# Revit family: Security_MasterStation_AiPhone_GT-C-H
name_source: partatom
category: Generic Models
units: mm (PartAtom-declared; Revit-internal decimal feet)

## family parameters
Can host rebar = No
Classification Number = 23.85.30.11.27
Cut with Voids When Loaded = No
Host = Face
Maintain Annotation Orientation = No
Part Type = Normal
Room Calculation Point = No
Round Connector Dimension = Use Diameter
Shared = No

## types (9) — shared parameters
Assembly Code = D5030900
Camera Control Material = Plastic - Aiphone - Gray
Construction Details = http://www.arcat.com
Default Elevation = 0' - 0"
Faceplate Material = Plastic - Aiphone - White
Green Building-LEED = http://www.arcat.com
Installation-Fabrication = http://www.aiphone.com
Keynote = 13700
Manufacturer = Aiphone Corp.
Manufacturer Fax = 425-455-0071
Manufacturer Website = http://www.aiphone.com
Operating Temperature Range = 32 - 104 F
Power Source = Powered by Power Supply
Product Data = http://www.arcat.com
Revision = R1_2015-05
Sales Information = http://www.aiphone.com
Screen Material = Plastic - Aiphone - Black
Send Message = http://www.arcat.com
Specification = http://www.arcat.com
Standards Conformance = as Specified
Talk Button Material = Plastic - Aiphone - Black
URL = http://www.aiphone.com
zero-valued in all types: Expected Lifespan (Years), Maintenance Schedule (Months), Warranty Duration (Years)

## per-type parameters (varying)
| type | 2C | 2H | Description | Include Handheld | Model | Unit Depth | Unit Height | Unit Width |
| Sub Station with Hearing Aid Compatibility | No | Yes | Aiphone Video and Audio Submaster Tenant Station - GT-2H-L as Specified | No | GT-2H-L | 0' - 1 1/4" | 0' - 5 1/2" | 0' - 7 1/2" |
| Sub Station with Handset | No | Yes | Aiphone Video and Audio Submaster Tenant Station - GT-2H with Handset as Specified | Yes | GT-2H | 0' - 2 1/2" | 0' - 7 1/4" | 0' - 9 3/4" |
| Sub Station | No | Yes | Aiphone Video and Audio Submaster Tenant Station - GT-2H as Specified | No | GT-2H | 0' - 1 1/4" | 0' - 5 1/2" | 0' - 7 1/2" |
| Master Station with Hearing Aid Compatibility | Yes | No | Aiphone Video and Audio Master Tenant Station - GT-2C-L as Specified | No | GT-2C-L | 0' - 1 1/4" | 0' - 5 1/2" | 0' - 7 1/2" |
| Master Station with Handset | Yes | No | Aiphone Video and Audio Master Tenant Station - GT-2C with Handset as Specified | Yes | GT-2C | 0' - 2 1/2" | 0' - 7 1/4" | 0' - 9 3/4" |
| Master Station | Yes | No | Aiphone Video and Audio Master Tenant Station - GT-2C as Specified | No | GT-2C | 0' - 1 1/4" | 0' - 5 1/2" | 0' - 7 1/2" |
| Standalone Station with Hearing Aid Compatibility | No | No | Aiphone Video and Audio Tenant Station - GT-1C-L as Specified | No | GT-1C-L | 0' - 1 1/4" | 0' - 5 1/2" | 0' - 7 1/2" |
| Standalone Station with Handset | No | No | Aiphone Video and Audio Tenant Station - GT-1C with Handset as Specified | Yes | GT-1C | 0' - 2 1/2" | 0' - 7 1/4" | 0' - 9 3/4" |
| Standalone Station | No | No | Aiphone Video and Audio Tenant Station - GT-1C as Specified | No | GT-1C | 0' - 1 1/4" | 0' - 5 1/2" | 0' - 7 1/2" |

## geometry (parser evidence)
native form markers: Sweep x4
no freeform markers — native parametric forms only
